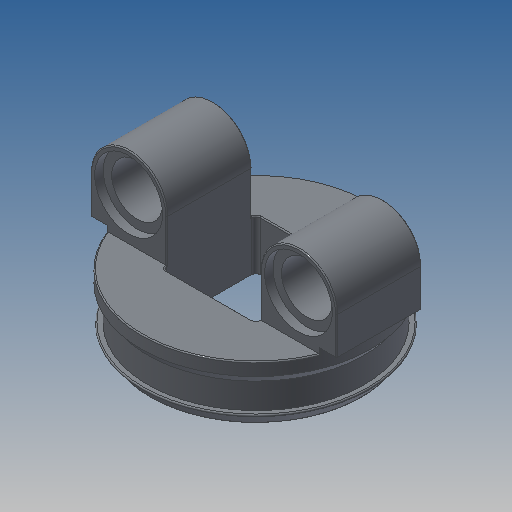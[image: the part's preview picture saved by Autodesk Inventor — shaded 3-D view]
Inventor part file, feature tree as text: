
AUTODESK INVENTOR PART (.ipt)
format: ipt  version: 2022.2 (Build 262287000, 287)  size: 382,976 bytes
history: native  units: in
note: dims shown in document units (in); Inventor stores cm internally (conversion verified against a paired STEP export)
features: sketch x6, extrude x6, revolve x1, plane x1, mirror x1, fillet x1, projected_geometry x1
ambient origin geometry x8: Origin, YZ Plane, XZ Plane, XY Plane, X Axis, Y Axis, Z Axis, Center Point
bodies: Solid1 (feature_tree)
feature tree (17):
  revolve  "Revolution1"  [1 undecoded]
  plane  "Work Plane1"
  sketch  "Sketch3"  dims[d2=0.7795in d3=0.8504in]
  extrude  "Extrusion1"  Depth=0.8504in
  extrude  "Extrusion2"  Depth=0.0472in
  extrude  "Extrusion3"  Depth=0.0472in
  extrude  "Extrusion4"  Depth=0.1575in
  extrude  "Extrusion5"  [1 undecoded]
  extrude  "Extrusion6"  Depth=0.0157in
  mirror  "Mirror1"
  fillet  "Fillet1"  Radius=0.3465in
  sketch  "Sketch2"  dims[d0=0.8504in d1=0.7276in]
  sketch  "Sketch4"  dims[d4=0.0472in d5=0.0945in]
  sketch  "Sketch5"  dims[d6=0.0236in d7=0.0472in]
  sketch  "Sketch6"  dims[d8=0.2205in d9=0.1575in]
  sketch  "Sketch7"  dims[d10=90.0deg d11=-0.0315in d12=0.0157in d13=0.3465in d14=0.0472in d15=0.3937in d16=0.0in d17=0.3937in d18=0.0in d19=0.189in d20=0.2835in d21=0.6299in d22=0.1575in d23=0.0157in d24=0.315in d25=0.0in d26=0.315in d27=0.0in d28=0.1883in d29=0.063in d30=0.0in d31=0.252in d32=0.0315in d33=0.0in d34=0.0039in]
  projected_geometry  "Projected Loop1"
note: 2 required parameter values undecoded (feature->parameter linkage not recoverable at this tier; creation-order binding heuristic only, values carry confidence <= 0.55)